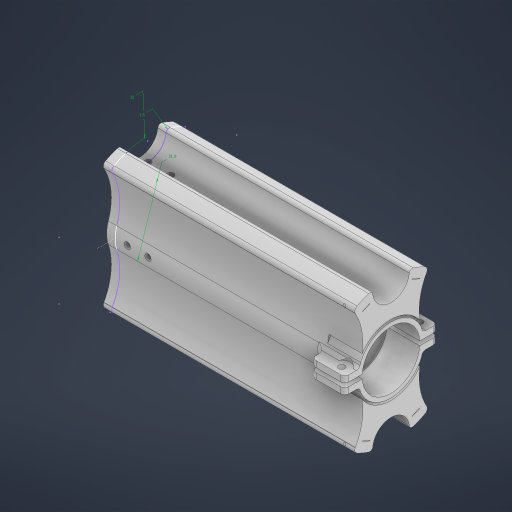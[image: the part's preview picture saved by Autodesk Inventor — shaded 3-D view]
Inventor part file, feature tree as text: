
AUTODESK INVENTOR PART (.ipt)
format: ipt  version: 2024.2 (Build 282272000, 272)  size: 1,199,104 bytes
history: native  units: in
note: dims shown in document units (in); Inventor stores cm internally (conversion verified against a paired STEP export)
features: extrude x21, sketch x19, mirror x7, projected_geometry x6, fillet x3, chamfer x1
ambient origin geometry x8: Origin, YZ Plane, XZ Plane, XY Plane, X Axis, Y Axis, Z Axis, Center Point
bodies: Solid1 (feature_tree)
feature tree (57):
  extrude  "Extrusion1"  Depth=0.0394in
  extrude  "Extrusion2"  Depth=0.0787in
  mirror  "Mirror1"
  fillet  "Fillet1"  Radius=0.0394in
  extrude  "Extrusion3"  Depth=0.1969in
  sketch  "Sketch4"  dims[d9=0.1181in d10=0.1378in d11=0.2756in]
  extrude  "Extrusion4"  Depth=0.1181in
  fillet  "Fillet2"  Radius=0.2756in
  extrude  "Extrusion5"  Depth=0.0787in
  sketch  "Sketch6"  dims[d15=0.3819in d16=0.1654in d17=0.0in]
  sketch  "Sketch7"  dims[d18=0.1181in d19=1.0945in]
  extrude  "Extrusion6"  Depth=0.1654in TaperAngle=0.0deg
  extrude  "Extrusion7"  Depth=0.1181in
  extrude  "Extrusion8"  Depth=0.0787in
  extrude  "Extrusion10"  Depth=0.1575in
  mirror  "Mirror4"
  mirror  "Mirror5"
  extrude  "Extrusion12"  Depth=0.0787in
  extrude  "Extrusion11"  Depth=2.7559in
  extrude  "Extrusion13"  Depth=0.3937in
  extrude  "Extrusion14"  Depth=1.9685in
  extrude  "Extrusion15"  Depth=0.0591in
  mirror  "Mirror6"
  mirror  "Mirror7"
  extrude  "Extrusion16"  Depth=4.6457in TaperAngle=0.0deg
  extrude  "Extrusion17"  Depth=0.3937in TaperAngle=0.0deg
  extrude  "Extrusion18"  Depth=1.3386in
  extrude  "Extrusion19"  Depth=0.0394in
  extrude  "Extrusion20"  Depth=0.3937in TaperAngle=0.0deg
  chamfer  "Chamfer1"  [1 undecoded]
  fillet  "Fillet3"  Radius=0.0079in
  extrude  "Extrusion21"  Depth=0.7874in
  extrude  "Extrusion9"  Depth=0.1181in
  mirror  "Mirror2"
  mirror  "Mirror3"
  sketch  "Sketch1"  dims[d0=1.0945in d1=0.0394in]
  sketch  "Sketch2"  dims[d3=0.1181in d4=0.0787in d5=0.0394in]
  sketch  "Sketch3"  dims[d6=0.6299in d7=0.0in d8=0.1969in]
  sketch  "Sketch5"  dims[d12=0.6299in d13=0.0in d14=0.0787in]
  sketch  "Sketch8"  dims[d20=0.0787in d21=1.252in]
  projected_geometry  "Projected Loop1"
  projected_geometry  "Projected Loop2"
  sketch  "Sketch10"  dims[d22=0.3937in d23=0.0in d24=0.1575in]
  sketch  "Sketch11"  dims[d25=0.1575in d26=0.0787in]
  projected_geometry  "Projected Loop3"
  sketch  "Sketch12"  dims[d27=3.4567in d28=0.0in d29=2.7559in]
  projected_geometry  "Projected Loop4"
  sketch  "Sketch13"  dims[d30=0.3937in d31=0.3937in]
  sketch  "Sketch14"  dims[d32=2.7559in d33=1.9685in]
  sketch  "Sketch15"  dims[d36=1.378in d40=0.0591in]
  sketch  "Sketch16"  dims[d41=1.252in d42=4.6457in d43=0.0in]
  sketch  "Sketch17"  dims[d44=2.7559in d45=0.3937in d46=0.0in]
  projected_geometry  "Projected Loop5"
  projected_geometry  "Projected Loop6"
  sketch  "Sketch18"  dims[d47=5.8121in d48=0.0in d49=1.3386in]
  sketch  "Sketch19"  dims[d50=0.0689in d51=0.0394in]
  sketch  "Sketch20"  dims[d52=1.9685in d54=0.0825in d56=0.3937in d57=0.0in d58=0.0in d59=0.0in d63=0.0079in d64=0.3091in d65=0.1181in d66=0.3543in d67=0.0in d68=0.1575in d69=0.0in d70=0.35in d71=0.0787in d72=0.0in d73=1.1024in d74=0.0787in d75=0.0in d76=0.315in d77=0.3937in d78=0.0in d79=1.2598in d80=1.3386in d81=0.3937in d82=0.0in d83=0.7874in d84=0.0in d85=0.3937in d86=0.1181in d87=0.0in d88=0.0in d89=0.3937in d90=0.0in d91=0.5906in d92=0.0in d93=0.0in d94=0.1181in d96=0.3937in d97=0.1181in d98=0.0787in d99=0.0787in d100=45.0deg d101=0.0787in d102=0.1417in d103=0.7874in d104=0.0in]
note: 1 required parameter value undecoded (feature->parameter linkage not recoverable at this tier; creation-order binding heuristic only, values carry confidence <= 0.55)
